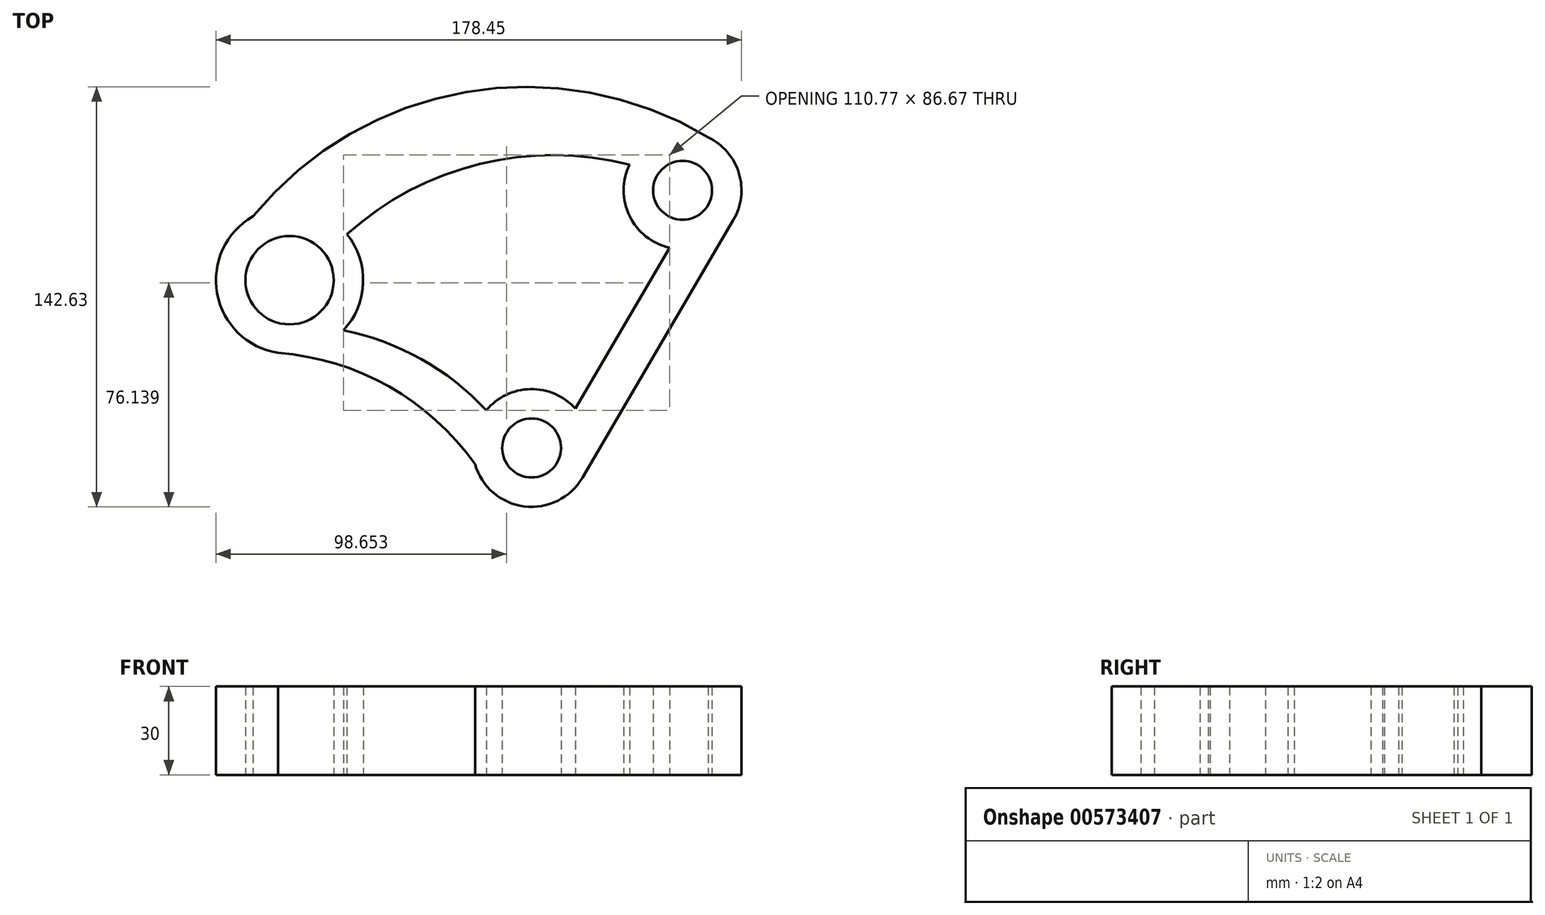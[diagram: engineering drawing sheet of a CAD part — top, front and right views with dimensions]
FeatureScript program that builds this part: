
annotation { "Feature Type Name" : "Feature", "Feature Type Description" : "" }
export const myFeature = defineFeature(function(context is Context, id is Id, definition is map)
    precondition{}
    {
        {
            var Q0;
            Q0=qCreatedBy(makeId("Top.planeOp"),FACE);
            var sketch = newSketch(context, id + "F0", { "sketchPlane" : qUnion([Q0])});
            skArc(sketch, "E0", {"start": v(17.3, 0) * mm, "mid": v(17.26, -17.4) * mm, "end": v(30.87, -28.25) * mm});
            skArc(sketch, "E1", {"start": v(-110.65, -17.6) * mm, "mid": v(-122.76, -43.8) * mm, "end": v(-102.1, -63.96) * mm});
            skArc(sketch, "E2", {"start": v(-35.25, -90.85) * mm, "mid": v(-23.8, -114.65) * mm, "end": v(1.27, -106.35) * mm});
            skCircle(sketch, "E3", {"center": v(35.28, -8.74) * mm, "radius": 10 * mm});
            skCircle(sketch, "E4", {"center": v(-15.99, -96.24) * mm, "radius": 10 * mm});
            skCircle(sketch, "E5", {"center": v(-98.17, -39.27) * mm, "radius": 15 * mm});
            skArc(sketch, "E6", {"start": v(44, 9.26) * mm, "mid": v(-38.32, 24.62) * mm, "end": v(-110.65, -17.6) * mm});
            skArc(sketch, "E7", {"start": v(40.14, 0) * mm, "mid": v(39.63, 0.25) * mm, "end": v(39.12, 0.5) * mm});
            skArc(sketch, "E8", {"start": v(17.3, 0) * mm, "mid": v(-33.65, 0.2) * mm, "end": v(-78.68, -23.6) * mm});
            skArc(sketch, "E9.trimOffspring", {"start": v(-79.9, -56.33) * mm, "mid": v(-73.19, -40.2) * mm, "end": v(-78.68, -23.6) * mm});
            skLineSegment(sketch, "E10", {"start": v(1.27, -106.35) * mm, "end": v(52.54, -18.85) * mm});
            skLineSegment(sketch, "E11", {"start": v(30.87, -28.25) * mm, "end": v(-1.13, -82.85) * mm});
            skArc(sketch, "E12.trimOffspring", {"start": v(52.54, -18.85) * mm, "mid": v(54.42, -2.93) * mm, "end": v(44, 9.26) * mm});
            skArc(sketch, "E13.trimOffspring", {"start": v(-1.13, -82.85) * mm, "mid": v(-22.52, -77.34) * mm, "end": v(-35.94, -94.89) * mm});
            skArc(sketch, "E14", {"start": v(-35.2, -101.77) * mm, "mid": v(-64.41, -75.37) * mm, "end": v(-102.1, -63.96) * mm});
            skArc(sketch, "E15", {"start": v(-31.35, -83.44) * mm, "mid": v(-53.48, -66.04) * mm, "end": v(-79.9, -56.33) * mm});
            skSolve(sketch);
        }
        {
            var Q0;
            Q0 = qSketchRegion(id + "F0", true);
            extrude(context, id + "F1", {"entities" : qUnion([Q0]), "depth" : 30 * mm, "offsetDistance" : 25 * mm});
        }
    });
